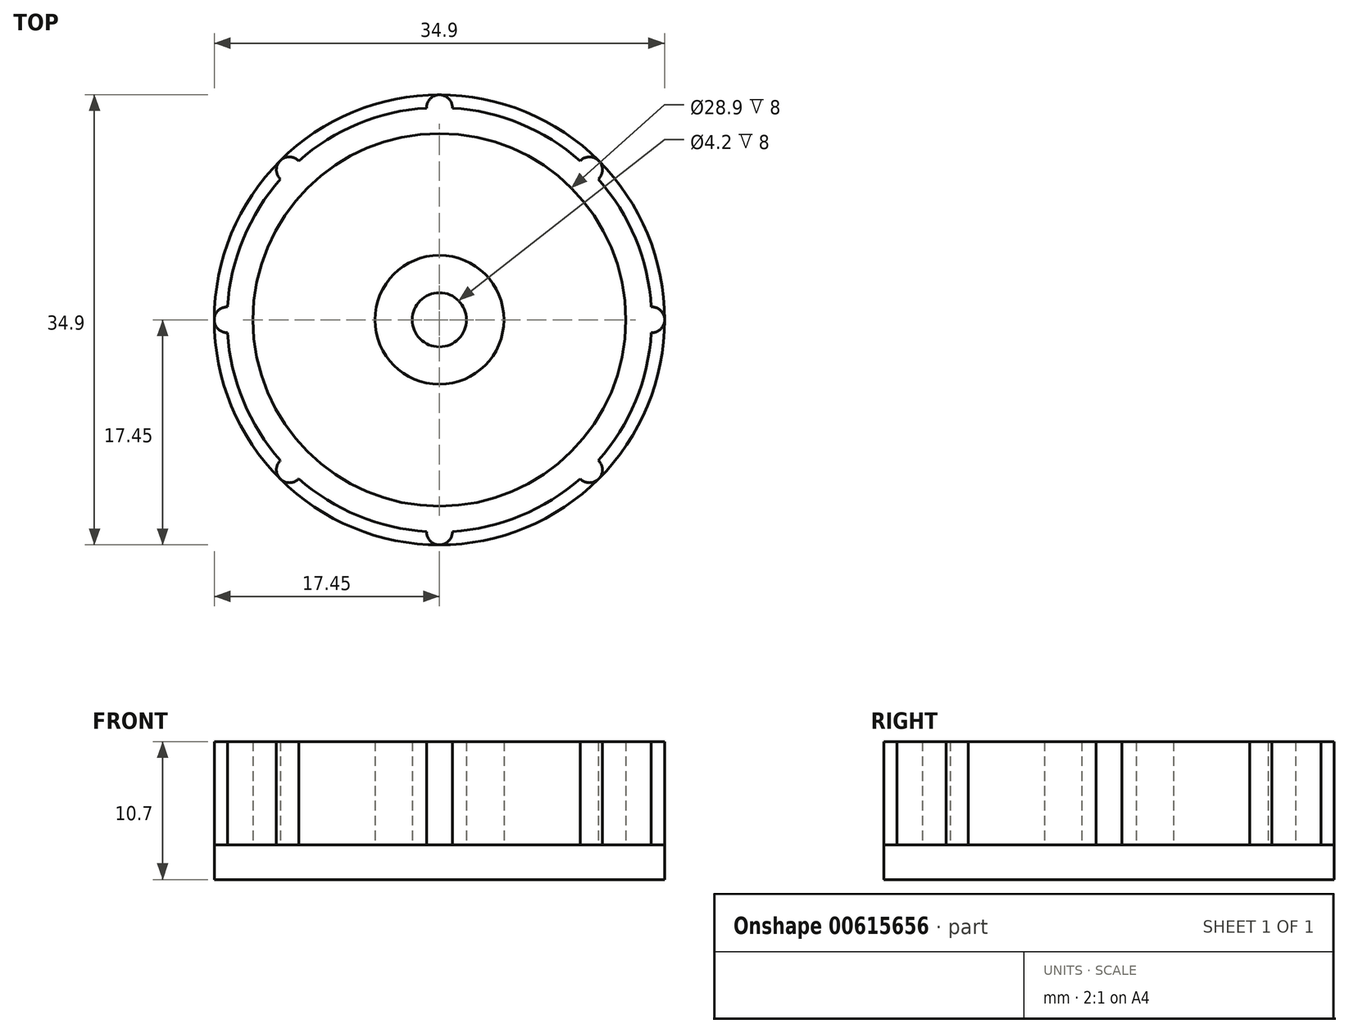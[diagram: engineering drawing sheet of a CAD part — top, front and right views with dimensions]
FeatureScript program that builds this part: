
annotation { "Feature Type Name" : "Feature", "Feature Type Description" : "" }
export const myFeature = defineFeature(function(context is Context, id is Id, definition is map)
    precondition{}
    {
        {
            var Q0;
            Q0=qCreatedBy(makeId("Top.planeOp"),FACE);
            var sketch = newSketch(context, id + "F0", { "sketchPlane" : qUnion([Q0])});
            skCircle(sketch, "E0", {"center": v(0, 0) * mm, "radius": 17.45 * mm});
            skSolve(sketch);
        }
        {
            var Q0;
            Q0 = qSketchRegion(id + "F0", true);
            extrude(context, id + "F1", {"entities" : qUnion([Q0]), "depth" : 2.7 * mm, "offsetDistance" : 25 * mm});
        }
        {
            var Q0;
            Q0=makeQuery(id+"F1.opExtrude","CAP_FACE",FACE,{"disambiguationData":[OSD([sQuery(id+"F0.wireOp",EDGE,"E0")])],"isStart":false});
            var sketch = newSketch(context, id + "F2", { "sketchPlane" : qUnion([Q0])});
            skCircle(sketch, "E1", {"center": v(0, 0) * mm, "radius": 16.45 * mm});
            skCircle(sketch, "E2", {"center": v(0, 0) * mm, "radius": 14.45 * mm});
            skCircle(sketch, "E3", {"center": v(0, 16.45) * mm, "radius": 1 * mm});
            skCircle(sketch, "E4.1.0", {"center": v(-11.63, 11.63) * mm, "radius": 1 * mm});
            skCircle(sketch, "E4.2.0", {"center": v(-16.45, 0) * mm, "radius": 1 * mm});
            skCircle(sketch, "E5.1.3.0", {"center": v(-11.63, -11.63) * mm, "radius": 1 * mm});
            skCircle(sketch, "E5.1.4.0", {"center": v(0, -16.45) * mm, "radius": 1 * mm});
            skCircle(sketch, "E5.1.5.0", {"center": v(11.63, -11.63) * mm, "radius": 1 * mm});
            skCircle(sketch, "E5.1.6.0", {"center": v(16.45, 0) * mm, "radius": 1 * mm});
            skCircle(sketch, "E5.1.7.0", {"center": v(11.63, 11.63) * mm, "radius": 1 * mm});
            skSolve(sketch);
        }
        {
            var Q0;
            Q0 = qSketchRegion(id + "F2", true);
            extrude(context, id + "F3", {"entities" : qUnion([Q0]), "operationType" : NewBodyOperationType.ADD, "depth" : 8 * mm, "offsetDistance" : 25 * mm});
        }
        {
            var Q0;
            Q0=makeQuery(id+"F3.boolean.opBoolean","SPLIT",FACE,{"disambiguationData":[TD([makeQuery(id+"F3.opExtrude","SWEPT_FACE",FACE,{"disambiguationData":[OSD([sQuery(id+"F2.wireOp",EDGE,"E2")])]})])],"derivedFrom":makeQuery(id+"F1.opExtrude","CAP_FACE",FACE,{"disambiguationData":[OSD([sQuery(id+"F0.wireOp",EDGE,"E0")])],"isStart":false})});
            var sketch = newSketch(context, id + "F4", { "sketchPlane" : qUnion([Q0])});
            skCircle(sketch, "E6", {"center": v(0, 0) * mm, "radius": 2.1 * mm});
            skCircle(sketch, "E7", {"center": v(0, 0) * mm, "radius": 5 * mm});
            skSolve(sketch);
        }
        {
            var Q0;
            Q0=makeQuery(id+"F4.imprint","IMPRINT",FACE,{"disambiguationData":[TD([[makeQuery(id+"F4.imprint","IMPRINT",EDGE,{"derivedFrom":sQuery(id+"F4.wireOp",EDGE,"E6")}),-1.0]])]});
            extrude(context, id + "F5", {"entities" : qUnion([Q0]), "operationType" : NewBodyOperationType.ADD, "depth" : 8 * mm, "offsetDistance" : 25 * mm});
        }
    });
